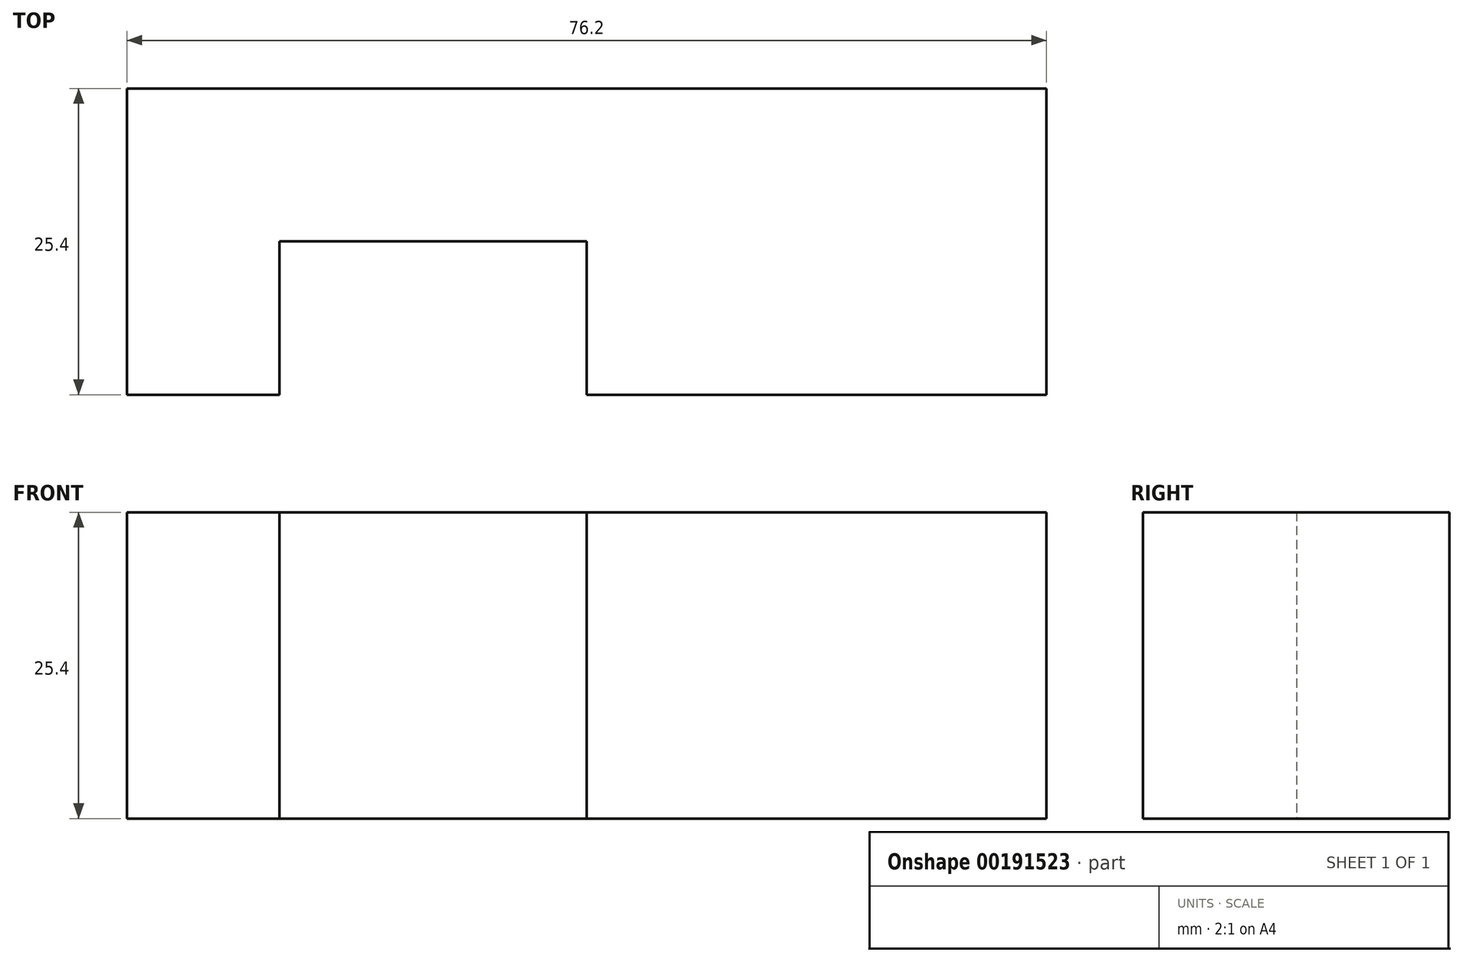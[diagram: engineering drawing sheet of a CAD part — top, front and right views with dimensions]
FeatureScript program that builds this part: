
annotation { "Feature Type Name" : "Feature", "Feature Type Description" : "" }
export const myFeature = defineFeature(function(context is Context, id is Id, definition is map)
    precondition{}
    {
        {
            var Q0;
            Q0=qCreatedBy(makeId("Top.planeOp"),FACE);
            var sketch = newSketch(context, id + "F0", { "sketchPlane" : qUnion([Q0])});
            skLineSegment(sketch, "E0.bottom", {"start": v(0, 0) * mm, "end": v(76.2, 0) * mm});
            skLineSegment(sketch, "E0.top", {"start": v(0, 25.4) * mm, "end": v(76.2, 25.4) * mm});
            skLineSegment(sketch, "E0.left", {"start": v(0, 0) * mm, "end": v(0, 25.4) * mm});
            skLineSegment(sketch, "E0.right", {"start": v(76.2, 0) * mm, "end": v(76.2, 25.4) * mm});
            skSolve(sketch);
        }
        {
            var Q0;
            Q0=makeQuery(id+"F0.imprint","IMPRINT",FACE,{"disambiguationData":[TD([[makeQuery(id+"F0.imprint","IMPRINT",EDGE,{"derivedFrom":sQuery(id+"F0.wireOp",EDGE,"E0.bottom")}),1.0]])]});
            extrude(context, id + "F1", {"entities" : qUnion([Q0]), "depth" : 25.4 * mm});
        }
        {
            var Q0;
            Q0=qCreatedBy(makeId("Front.planeOp"),FACE);
            var sketch = newSketch(context, id + "F2", { "sketchPlane" : qUnion([Q0])});
            skLineSegment(sketch, "E1.bottom", {"start": v(25.37, 25.82) * mm, "end": v(50.83, 25.82) * mm});
            skLineSegment(sketch, "E1.top", {"start": v(25.37, 13.1) * mm, "end": v(50.83, 13.1) * mm});
            skLineSegment(sketch, "E1.left", {"start": v(25.37, 25.82) * mm, "end": v(25.37, 13.1) * mm});
            skLineSegment(sketch, "E1.right", {"start": v(50.83, 25.82) * mm, "end": v(50.83, 13.1) * mm});
            skSolve(sketch);
        }
        {
            var Q0;
            Q0=makeQuery(id+"F2.imprint","IMPRINT",FACE,{"disambiguationData":[TD([[makeQuery(id+"F2.imprint","IMPRINT",EDGE,{"derivedFrom":sQuery(id+"F2.wireOp",EDGE,"E1.bottom")}),-1.0]])]});
            extrude(context, id + "F3", {"entities" : qUnion([Q0]), "operationType" : NewBodyOperationType.REMOVE, "oppositeDirection" : true, "depth" : 25.4 * mm});
        }
        {
            var Q0;
            Q0=qCreatedBy(makeId("Top.planeOp"),FACE);
            var sketch = newSketch(context, id + "F4", { "sketchPlane" : qUnion([Q0])});
            skLineSegment(sketch, "E2.bottom", {"start": v(12.65, 0) * mm, "end": v(38.1, 0) * mm});
            skLineSegment(sketch, "E2.top", {"start": v(12.65, 12.73) * mm, "end": v(38.1, 12.73) * mm});
            skLineSegment(sketch, "E2.left", {"start": v(12.65, 0) * mm, "end": v(12.65, 12.73) * mm});
            skLineSegment(sketch, "E2.right", {"start": v(38.1, 0) * mm, "end": v(38.1, 12.73) * mm});
            skSolve(sketch);
        }
        {
            var Q0;
            Q0=makeQuery(id+"F4.imprint","IMPRINT",FACE,{"disambiguationData":[TD([[makeQuery(id+"F4.imprint","IMPRINT",EDGE,{"derivedFrom":sQuery(id+"F4.wireOp",EDGE,"E2.bottom")}),1.0]])]});
            extrude(context, id + "F5", {"entities" : qUnion([Q0]), "operationType" : NewBodyOperationType.REMOVE, "depth" : 25.65 * mm});
        }
        {
            var Q0;
            Q0=makeQuery(id+"F3.boolean.opBoolean","COPY",FACE,{"derivedFrom":makeQuery(id+"F3.opExtrude","SWEPT_FACE",FACE,{"disambiguationData":[OSD([sQuery(id+"F2.wireOp",EDGE,"E1.top")])]})});
            var Q1;
            {var subQ0=sQuery(id+"F0.wireOp",EDGE,"E0.bottom");var subQ1=sQuery(id+"F0.wireOp",EDGE,"E0.top");var subQ2=sQuery(id+"F0.wireOp",EDGE,"E0.left");Q1=makeQuery(id+"F3.boolean.opBoolean","SPLIT",FACE,{"disambiguationData":[TD([makeQuery(id+"F1.opExtrude","SWEPT_FACE",FACE,{"disambiguationData":[OSD([subQ2])]})])],"derivedFrom":makeQuery(id+"F1.opExtrude","CAP_FACE",FACE,{"disambiguationData":[OSD([subQ0,subQ1,subQ2,sQuery(id+"F0.wireOp",EDGE,"E0.right")])],"isStart":false})});}
            extrude(context, id + "F6", {"entities" : qUnion([Q0]), "operationType" : NewBodyOperationType.ADD, "endBound" : BoundingType.UP_TO_SURFACE, "endBoundEntityFace" : qUnion([Q1]), "depth" : 25.4 * mm});
        }
    });
